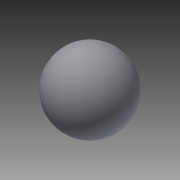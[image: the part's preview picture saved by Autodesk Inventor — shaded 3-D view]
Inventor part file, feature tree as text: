
AUTODESK INVENTOR PART (.ipt)
format: ipt  version: 2015 (Build 190159000, 159)  size: 102,400 bytes
history: native  units: in
note: dims shown in document units (in); Inventor stores cm internally (conversion verified against a paired STEP export)
features: revolve x1, sketch x1
ambient origin geometry x8: Origin, YZ Plane, XZ Plane, XY Plane, X Axis, Y Axis, Z Axis, Center Point
bodies: Solid1 (feature_tree)
feature tree (2):
  revolve  "Revolution1"  Angle=90.0deg
  sketch  "Sketch1"  dims[d0=0.2in d1=90.0deg]
